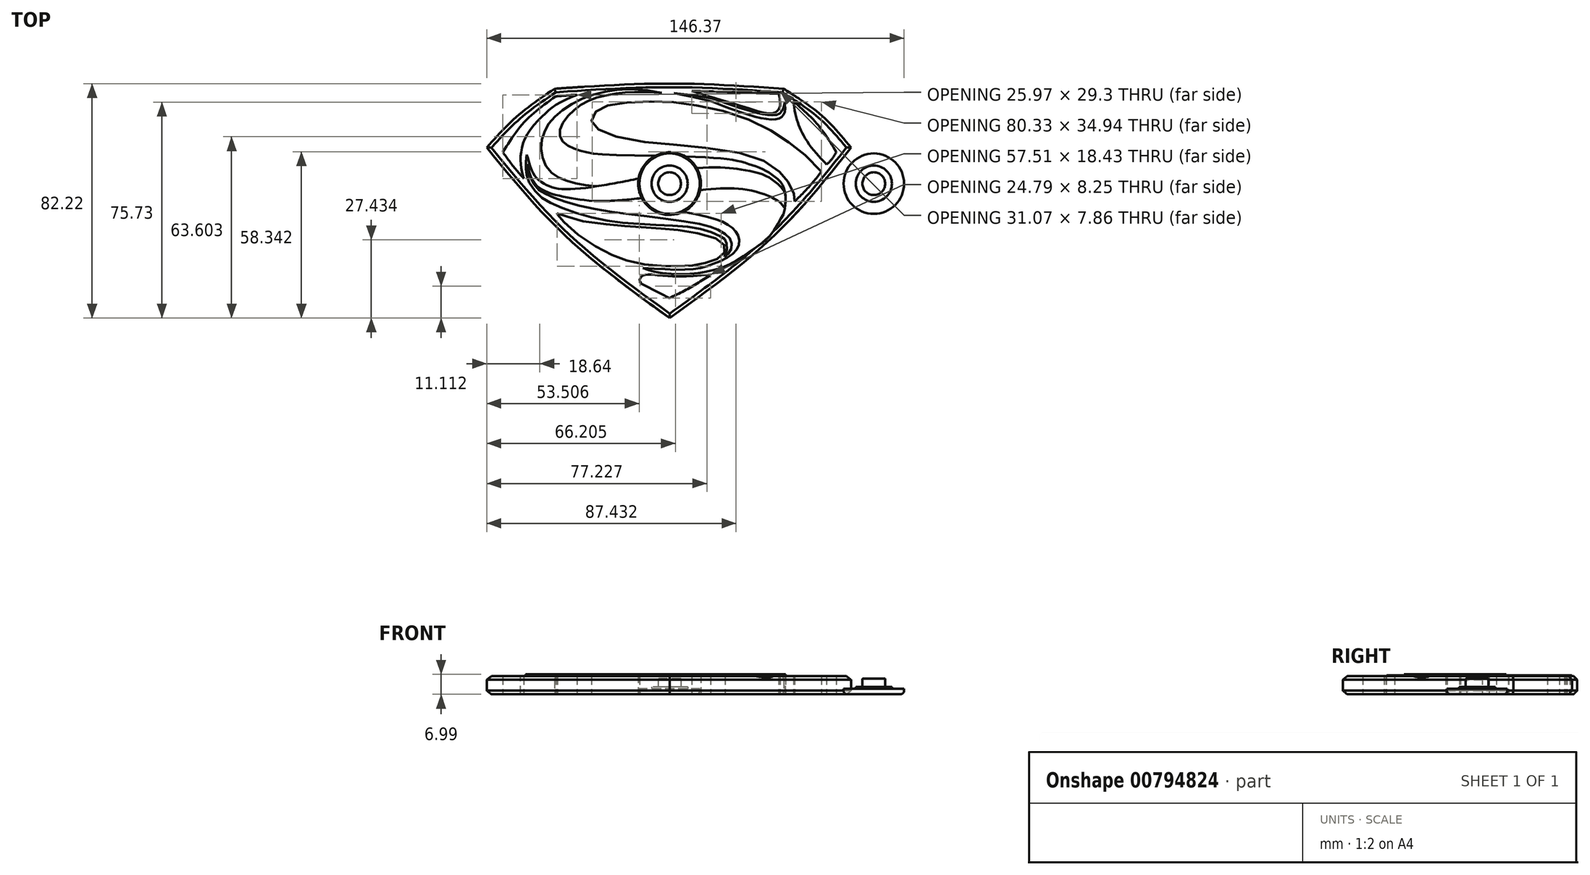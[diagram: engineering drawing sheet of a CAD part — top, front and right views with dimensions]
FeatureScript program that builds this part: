
annotation { "Feature Type Name" : "Feature", "Feature Type Description" : "" }
export const myFeature = defineFeature(function(context is Context, id is Id, definition is map)
    precondition{}
    {
        {
            var Q0;
            Q0=qCreatedBy(makeId("Top.planeOp"),FACE);
            var sketch = newSketch(context, id + "F0", { "sketchPlane" : qUnion([Q0])});
            skCircle(sketch, "E0", {"center": v(0, 0) * mm, "radius": 10.99 * mm});
            skPoint(sketch, "E1", {"position": v(-64.14, 12.66) * mm});
            skPoint(sketch, "E2", {"position": v(-40.37, 33.3) * mm});
            skPoint(sketch, "E3", {"position": v(40.02, 33.3) * mm});
            skPoint(sketch, "E4", {"position": v(63.66, 12.66) * mm});
            skPoint(sketch, "E5", {"position": v(0, -47.12) * mm});
            skPoint(sketch, "E6", {"position": v(7.76, 32.54) * mm});
            skPoint(sketch, "E7", {"position": v(38.28, 31.5) * mm});
            skPoint(sketch, "E8", {"position": v(43.45, 28.9) * mm});
            skPoint(sketch, "E9", {"position": v(55.1, 6.77) * mm});
            skPoint(sketch, "E10", {"position": v(58.48, 11.04) * mm});
            skPoint(sketch, "E11", {"position": v(-51.19, 1.83) * mm});
            skPoint(sketch, "E12", {"position": v(-39.94, 30.62) * mm});
            skPoint(sketch, "E13", {"position": v(-32.52, 31.13) * mm});
            skPoint(sketch, "E14", {"position": v(-39.39, -10.47) * mm});
            skPoint(sketch, "E15", {"position": v(43.9, -6.25) * mm});
            skPoint(sketch, "E16", {"position": v(53.25, 4.2) * mm});
            skPoint(sketch, "E17", {"position": v(14.46, -31.93) * mm});
            skPoint(sketch, "E18", {"position": v(-0.08, -40.13) * mm});
            skPoint(sketch, "E19", {"position": v(-58.48, 11.01) * mm});
            skPoint(sketch, "E20", {"position": v(-50.07, 10.18) * mm});
            skPoint(sketch, "E21", {"position": v(-49.83, 6.88) * mm});
            skPoint(sketch, "E22", {"position": v(19.28, -25.63) * mm});
            skPoint(sketch, "E23", {"position": v(-9.37, -29.55) * mm});
            skPoint(sketch, "E24", {"position": v(40.4, 28.63) * mm});
            skPoint(sketch, "E25", {"position": v(40.4, -8.67) * mm});
            skPoint(sketch, "E26", {"position": v(-2.68, 31.88) * mm});
            skPoint(sketch, "E27", {"position": v(0, 31.88) * mm});
            skFitSpline(sketch, "E28", {"points": [v(-40.37, 33.3) * mm, v(0, 35.1) * mm, v(40.02, 33.3) * mm], "startDerivative": vector(80.66, 5.4) * mm, "endDerivative": vector(80.13, -5.42) * mm});
            skFitSpline(sketch, "E29", {"points": [v(40.02, 33.3) * mm, v(53.16, 24.07) * mm, v(63.66, 12.66) * mm], "startDerivative": vector(27.5, -18.05) * mm, "endDerivative": vector(20.1, -24.17) * mm});
            skFitSpline(sketch, "E30", {"points": [v(63.66, 12.66) * mm, v(36.43, -18.47) * mm, v(0, -47.12) * mm], "startDerivative": vector(-52.44, -66.14) * mm, "endDerivative": vector(-74.66, -53.56) * mm});
            skFitSpline(sketch, "E31", {"points": [v(0, -47.12) * mm, v(-36.36, -18.47) * mm, v(-64.14, 12.66) * mm], "startDerivative": vector(-74.42, 53.78) * mm, "endDerivative": vector(-53.67, 65.9) * mm});
            skFitSpline(sketch, "E32", {"points": [v(-64.14, 12.66) * mm, v(-53.44, 23.64) * mm, v(-40.37, 33.3) * mm], "startDerivative": vector(20.7, 23.07) * mm, "endDerivative": vector(26.78, 18.22) * mm});
            skFitSpline(sketch, "E33", {"points": [v(-39.94, 30.62) * mm, v(-50.69, 21.87) * mm, v(-58.48, 11.01) * mm], "startDerivative": vector(-22.95, -16.13) * mm, "endDerivative": vector(-14.34, -23.1) * mm});
            skFitSpline(sketch, "E34", {"points": [v(-39.94, 30.62) * mm, v(-36.36, 30.92) * mm, v(-32.52, 31.13) * mm], "startDerivative": vector(6.93, 0.72) * mm, "endDerivative": vector(6.91, 0.08) * mm});
            skFitSpline(sketch, "E35", {"points": [v(-58.48, 11.01) * mm, v(-55.4, 6.86) * mm, v(-51.19, 1.83) * mm], "startDerivative": vector(6.2, -8.69) * mm, "endDerivative": vector(8.34, -9.65) * mm});
            skFitSpline(sketch, "E36", {"points": [v(-51.19, 1.83) * mm, v(-51.94, 4.77) * mm, v(-52.27, 8.5) * mm, v(-51.67, 12.97) * mm, v(-49.15, 18.56) * mm, v(-43.9, 24.34) * mm, v(-39.94, 27.57) * mm, v(-32.52, 31.13) * mm], "startDerivative": vector(-7.64, 26.31) * mm, "endDerivative": vector(46.02, 18.09) * mm});
            skFitSpline(sketch, "E37", {"points": [v(7.76, 32.54) * mm, v(18.66, 32.23) * mm, v(38.28, 31.5) * mm], "startDerivative": vector(23.67, -0.62) * mm, "endDerivative": vector(36.73, -1.42) * mm});
            skFitSpline(sketch, "E38", {"points": [v(38.28, 31.5) * mm, v(38.7, 29.67) * mm, v(38.66, 26.9) * mm, v(37.58, 25.39) * mm, v(36.42, 24.79) * mm, v(33.06, 24.83) * mm, v(28.22, 26.27) * mm, v(21.1, 28.47) * mm, v(7.76, 32.54) * mm], "startDerivative": vector(5.44, -19.74) * mm, "endDerivative": vector(-61.62, 18.92) * mm});
            skFitSpline(sketch, "E39", {"points": [v(43.45, 28.9) * mm, v(52.06, 20.57) * mm, v(58.48, 11.04) * mm], "startDerivative": vector(18.08, -15.79) * mm, "endDerivative": vector(11.96, -19.95) * mm});
            skFitSpline(sketch, "E40", {"points": [v(58.48, 11.04) * mm, v(56.98, 8.65) * mm, v(55.1, 6.77) * mm], "startDerivative": vector(-2.74, -4.94) * mm, "endDerivative": vector(-4.03, -3.6) * mm});
            skFitSpline(sketch, "E41", {"points": [v(55.1, 6.77) * mm, v(52.62, 9.33) * mm, v(49.02, 13.7) * mm, v(46.46, 17.85) * mm, v(45.14, 21.05) * mm, v(44.02, 24.73) * mm, v(43.45, 28.9) * mm], "startDerivative": vector(-15.43, 15.4) * mm, "endDerivative": vector(-2.63, 26.61) * mm});
            skFitSpline(sketch, "E42", {"points": [v(14.46, -31.93) * mm, v(7.31, -36.4) * mm, v(-0.08, -40.13) * mm], "startDerivative": vector(-14.08, -9.25) * mm, "endDerivative": vector(-15.01, -7.14) * mm});
            skFitSpline(sketch, "E43", {"points": [v(-0.08, -40.13) * mm, v(-9.4, -35.36) * mm, v(-10.21, -34.82) * mm, v(-10.48, -33.96) * mm, v(-10.15, -32.94) * mm, v(-9.13, -32.13) * mm, v(-7.55, -31.87) * mm, v(-2.45, -32.25) * mm, v(1.98, -32.55) * mm, v(7.03, -32.46) * mm, v(14.46, -31.93) * mm], "startDerivative": vector(-67.8, 34.66) * mm, "endDerivative": vector(3.78, 0.48) * mm});
            skFitSpline(sketch, "E44", {"points": [v(-39.39, -10.47) * mm, v(-36.9, -11.24) * mm, v(-31.58, -12.93) * mm, v(-18.82, -14.57) * mm, v(-12.34, -15.08) * mm, v(-2.67, -15.73) * mm, v(4.94, -16.53) * mm, v(15.15, -18.82) * mm, v(18.68, -20.8) * mm, v(19.36, -22.15) * mm, v(19.36, -23.68) * mm, v(18.1, -25.4) * mm, v(15.6, -26.9) * mm, v(11.3, -28.07) * mm, v(7.09, -28.83) * mm, v(0.64, -28.97) * mm, v(-5.78, -28.66) * mm, v(-14.27, -27.19) * mm, v(-20.2, -24.98) * mm, v(-28.78, -20.23) * mm, v(-36.56, -13.98) * mm, v(-39.24, -10.87) * mm, v(-39.32, -10.74) * mm], "startDerivative": vector(73.96, -20.72) * mm, "endDerivative": vector(-5.97, 11.97) * mm});
            skFitSpline(sketch, "E45", {"points": [v(-39.32, -10.74) * mm, v(-39.39, -10.57) * mm, v(-39.39, -10.47) * mm], "startDerivative": vector(-0.18, 0.22) * mm, "endDerivative": vector(0.04, 0.31) * mm});
            skFitSpline(sketch, "E46", {"points": [v(53.25, 4.2) * mm, v(49.19, -0.76) * mm, v(43.9, -6.25) * mm], "startDerivative": vector(-8.07, -10.34) * mm, "endDerivative": vector(-10.53, -10.36) * mm});
            skFitSpline(sketch, "E47", {"points": [v(43.9, -6.25) * mm, v(43.9, -5.44) * mm, v(43.77, -4.33) * mm, v(43.29, -2.76) * mm, v(41.52, 0.67) * mm, v(39.87, 2.87) * mm, v(35.73, 6.37) * mm, v(27.93, 9.93) * mm, v(7.68, 13.1) * mm, v(-8.05, 14.57) * mm, v(-21.85, 17.4) * mm, v(-25.64, 19.5) * mm, v(-27.06, 21.07) * mm, v(-27.3, 23.07) * mm, v(-26.38, 24.79) * mm, v(-24.06, 26.55) * mm, v(-20.02, 27.79) * mm, v(-11.62, 28.7) * mm, v(-1.38, 28.75) * mm, v(7.82, 27.7) * mm, v(20.5, 25.07) * mm, v(32.34, 20.39) * mm, v(40.34, 15.5) * mm, v(46.38, 11.1) * mm, v(53.25, 4.2) * mm], "startDerivative": vector(4.91, 51.7) * mm, "endDerivative": vector(132.4, -142.33) * mm});
            skFitSpline(sketch, "E48", {"points": [v(40.4, 28.63) * mm, v(40.06, 27.03) * mm, v(39.45, 25.6) * mm, v(38.15, 24.37) * mm, v(35.2, 24.05) * mm, v(31.42, 24.69) * mm, v(24.88, 26.45) * mm, v(19.2, 28.46) * mm, v(14.9, 29.85) * mm, v(8.9, 30.88) * mm, v(1.53, 31.72) * mm], "startDerivative": vector(-3.32, -25.72) * mm, "endDerivative": vector(-54.65, 5.86) * mm});
            skFitSpline(sketch, "E49", {"points": [v(40.4, 28.63) * mm, v(40.5, 27.43) * mm, v(40.52, 25.95) * mm, v(40.2, 24.52) * mm, v(39.55, 23.59) * mm, v(38.69, 22.97) * mm, v(37.25, 22.55) * mm, v(34.59, 22.59) * mm, v(30.57, 23.33) * mm, v(24.5, 25.22) * mm, v(20.17, 26.73) * mm, v(15.83, 28.4) * mm, v(11.85, 29.6) * mm, v(1.53, 31.72) * mm], "startDerivative": vector(3.06, -23.78) * mm, "endDerivative": vector(-90.61, 18.57) * mm});
            skFitSpline(sketch, "E50", {"points": [v(-2.68, 31.88) * mm, v(-7.95, 32.74) * mm, v(-17.45, 32.96) * mm, v(-30.23, 29.97) * mm, v(-39.96, 23.74) * mm, v(-44.1, 17.75) * mm, v(-44.83, 10.28) * mm, v(-41.26, 3.66) * mm, v(-34.87, 0.66) * mm, v(-25.14, -0.98) * mm, v(-17.45, -1.32) * mm, v(-18.98, -2.45) * mm, v(-32.6, -3.3) * mm, v(-31.7, -4.65) * mm, v(-21.24, -6.69) * mm, v(-12.19, -7.76) * mm, v(11.4, -11.16) * mm, v(20.9, -14.67) * mm, v(23.56, -17.32) * mm, v(24.41, -20.66) * mm, v(22.32, -24.45) * mm, v(15.13, -28.24) * mm, v(7.33, -30.05) * mm, v(-9.37, -29.55) * mm], "startDerivative": vector(-142.44, 17.07) * mm, "endDerivative": vector(-293.82, 20.27) * mm});
            skFitSpline(sketch, "E51", {"points": [v(-9.37, -29.55) * mm, v(-4.88, -30.97) * mm, v(5.35, -31.7) * mm, v(14.06, -30.62) * mm, v(21.7, -28.02) * mm, v(29, -23.2) * mm, v(35.18, -18.41) * mm, v(38.8, -12.68) * mm, v(40.21, -9.83) * mm, v(40.16, -1.79) * mm, v(36.4, 2.85) * mm, v(32.12, 5.3) * mm, v(26.56, 7.28) * mm, v(15.88, 9.03) * mm, v(-22.44, 10.23) * mm, v(-29.79, 11.13) * mm, v(-34.2, 12.6) * mm, v(-37.8, 15.33) * mm, v(-38.3, 19.43) * mm, v(-33.85, 25.5) * mm, v(-27.24, 29.56) * mm, v(-17.42, 31.74) * mm, v(-2.68, 31.88) * mm], "startDerivative": vector(111.61, -43.93) * mm, "endDerivative": vector(382.73, -23.2) * mm});
            skFitSpline(sketch, "E52", {"points": [v(40.4, -8.67) * mm, v(40.7, -5.87) * mm, v(40.56, -3.55) * mm, v(39.02, -1.13) * mm, v(35.74, 1.6) * mm, v(31.47, 3.62) * mm, v(24.9, 4.98) * mm, v(19.45, 5.6) * mm, v(8.3, 5.35) * mm, v(-3.53, 3.33) * mm, v(-13.8, 1.18) * mm, v(-22.74, -0.47) * mm, v(-33.27, -1.85) * mm, v(-39.9, -1.61) * mm, v(-42.99, -0.54) * mm, v(-46.25, 1.58) * mm, v(-48.17, 4.27) * mm, v(-50.07, 10.18) * mm], "startDerivative": vector(13.14, 77.38) * mm, "endDerivative": vector(-29.7, 107.37) * mm});
            skFitSpline(sketch, "E53", {"points": [v(-50.07, 10.18) * mm, v(-50.35, 7.84) * mm, v(-50.42, 5.22) * mm, v(-50.15, 3.18) * mm, v(-49.15, 0.24) * mm, v(-46.14, -3.8) * mm, v(-42.38, -6.4) * mm, v(-34.14, -9.81) * mm, v(-22.18, -12.93) * mm, v(-9.5, -14.21) * mm, v(4.26, -14.95) * mm, v(12.52, -16.3) * mm, v(17.32, -18.25) * mm, v(19.08, -19.25) * mm, v(19.64, -19.91) * mm, v(20.02, -21.2) * mm, v(20.08, -22.93) * mm, v(19.28, -25.63) * mm], "startDerivative": vector(-7.56, -53.6) * mm, "endDerivative": vector(-22.29, -60.92) * mm});
            skFitSpline(sketch, "E54", {"points": [v(19.28, -25.63) * mm, v(20.18, -24.97) * mm, v(21.42, -23.31) * mm, v(21.72, -21.43) * mm, v(21.5, -19.71) * mm, v(20.16, -18.13) * mm, v(16.78, -16.11) * mm, v(12.06, -14.45) * mm, v(-5.28, -11.81) * mm, v(-24.12, -9.3) * mm, v(-37.8, -5.93) * mm, v(-43.72, -3.47) * mm, v(-46.44, -1.63) * mm, v(-49, 2.57) * mm, v(-49.52, 4.4) * mm, v(-49.83, 6.88) * mm], "startDerivative": vector(26.73, 16.6) * mm, "endDerivative": vector(-6.33, 54.96) * mm});
            skFitSpline(sketch, "E55", {"points": [v(-49.83, 6.88) * mm, v(-49.04, 3.5) * mm, v(-47.4, 0.29) * mm, v(-45.66, -1.45) * mm, v(-42.08, -3.3) * mm, v(-36.7, -4.66) * mm, v(-30.44, -5.7) * mm, v(-18.92, -5.95) * mm, v(7.7, -2.71) * mm, v(20.26, -1.63) * mm, v(29.3, -2.6) * mm, v(36.52, -5.15) * mm, v(39.24, -7.07) * mm, v(40.4, -8.67) * mm], "startDerivative": vector(10.3, -60.65) * mm, "endDerivative": vector(23.49, -38.16) * mm});
            skSolve(sketch);
        }
        {
            var Q0;
            Q0=makeQuery(id+"F0.imprint","IMPRINT",FACE,{"disambiguationData":[TD([[makeQuery(id+"F0.imprint","IMPRINT",EDGE,{"derivedFrom":sQuery(id+"F0.wireOp",EDGE,"E28")}),-1.0]])]});
            var Q1;
            {var subQ0=sQuery(id+"F0.wireOp",EDGE,"E55");var subQ1=sQuery(id+"F0.wireOp",EDGE,"E0");var subQ2=makeQuery(id+"F0.imprint","INTERSECT",VERTEX,{"disambiguationData":[OD(0.0)],"derivedFrom":[subQ1,subQ0]});Q1=makeQuery(id+"F0.imprint","IMPRINT",FACE,{"disambiguationData":[TD([[makeQuery(id+"F0.imprint","IMPRINT",EDGE,{"disambiguationData":[TD([[subQ2,-1.0]])],"derivedFrom":subQ1}),-1.0]])]});}
            extrude(context, id + "F1", {"entities" : qUnion([Q0, Q1]), "depth" : 6.35 * mm, "offsetDistance" : 25.4 * mm});
        }
        {
            var Q0;
            {var subQ5=sQuery(id+"F0.wireOp",EDGE,"E0");var subQ7=sQuery(id+"F0.wireOp",EDGE,"E50");var subQ9=makeQuery(id+"F0.imprint","INTERSECT",VERTEX,{"disambiguationData":[OD(1.0)],"derivedFrom":[subQ5,subQ7]});Q0=makeQuery(id+"F0.imprint","IMPRINT",FACE,{"disambiguationData":[TD([[makeQuery(id+"F0.imprint","IMPRINT",EDGE,{"disambiguationData":[TD([[subQ9,-1.0]])],"derivedFrom":subQ5}),-1.0]])]});}
            var Q1;
            {var subQ0=sQuery(id+"F0.wireOp",EDGE,"E51");var subQ1=sQuery(id+"F0.wireOp",EDGE,"E0");var subQ2=makeQuery(id+"F0.imprint","INTERSECT",VERTEX,{"disambiguationData":[OD(0.0)],"derivedFrom":[subQ1,subQ0]});Q1=makeQuery(id+"F0.imprint","IMPRINT",FACE,{"disambiguationData":[TD([[makeQuery(id+"F0.imprint","IMPRINT",EDGE,{"disambiguationData":[TD([[subQ2,1.0]])],"derivedFrom":subQ1}),-1.0]])]});}
            var Q2;
            {var subQ0=sQuery(id+"F0.wireOp",EDGE,"E51");var subQ1=sQuery(id+"F0.wireOp",EDGE,"E0");var subQ2=makeQuery(id+"F0.imprint","INTERSECT",VERTEX,{"disambiguationData":[OD(1.0)],"derivedFrom":[subQ1,subQ0]});Q2=makeQuery(id+"F0.imprint","IMPRINT",FACE,{"disambiguationData":[TD([[makeQuery(id+"F0.imprint","IMPRINT",EDGE,{"disambiguationData":[TD([[subQ2,-1.0]])],"derivedFrom":subQ1}),-1.0]])]});}
            var Q3;
            Q3=makeQuery(id+"F0.imprint","IMPRINT",FACE,{"disambiguationData":[TD([[makeQuery(id+"F0.imprint","IMPRINT",EDGE,{"derivedFrom":sQuery(id+"F0.wireOp",EDGE,"E48")}),1.0]])]});
            extrude(context, id + "F2", {"entities" : qUnion([Q0, Q1, Q2, Q3]), "operationType" : NewBodyOperationType.ADD, "depth" : 6.6 * mm, "offsetDistance" : 25.4 * mm});
        }
        {
            var Q0;
            {var subQ1=sQuery(id+"F0.wireOp",EDGE,"E53");Q0=makeQuery(id+"F0.imprint","IMPRINT",FACE,{"disambiguationData":[TD([[makeQuery(id+"F0.imprint","IMPRINT",EDGE,{"derivedFrom":subQ1}),1.0]])]});}
            var Q1;
            {var subQ0=sQuery(id+"F0.wireOp",EDGE,"E52");var subQ1=sQuery(id+"F0.wireOp",EDGE,"E0");var subQ2=makeQuery(id+"F0.imprint","INTERSECT",VERTEX,{"disambiguationData":[OD(1.0)],"derivedFrom":[subQ1,subQ0]});Q1=makeQuery(id+"F0.imprint","IMPRINT",FACE,{"disambiguationData":[TD([[makeQuery(id+"F0.imprint","IMPRINT",EDGE,{"disambiguationData":[TD([[subQ2,-1.0]])],"derivedFrom":subQ1}),-1.0]])]});}
            var Q2;
            {var subQ1=sQuery(id+"F0.wireOp",EDGE,"E52");var subQ5=sQuery(id+"F0.wireOp",EDGE,"E0");var subQ6=makeQuery(id+"F0.imprint","INTERSECT",VERTEX,{"disambiguationData":[OD(0.0)],"derivedFrom":[subQ5,subQ1]});Q2=makeQuery(id+"F0.imprint","IMPRINT",FACE,{"disambiguationData":[TD([[makeQuery(id+"F0.imprint","IMPRINT",EDGE,{"disambiguationData":[TD([[subQ6,1.0]])],"derivedFrom":subQ5}),-1.0]])]});}
            extrude(context, id + "F3", {"entities" : qUnion([Q0, Q1, Q2]), "operationType" : NewBodyOperationType.ADD, "depth" : 7 * mm, "offsetDistance" : 25.4 * mm});
        }
        {
            var Q0;
            Q0=makeQuery(id+"F1.opExtrude","CAP_EDGE",EDGE,{"disambiguationData":[OSD([sQuery(id+"F0.wireOp",EDGE,"E32")])],"isStart":false});
            var Q1;
            Q1=makeQuery(id+"F1.opExtrude","CAP_EDGE",EDGE,{"disambiguationData":[OSD([sQuery(id+"F0.wireOp",EDGE,"E31")])],"isStart":false});
            var Q2;
            Q2=makeQuery(id+"F1.opExtrude","CAP_EDGE",EDGE,{"disambiguationData":[OSD([sQuery(id+"F0.wireOp",EDGE,"E30")])],"isStart":false});
            var Q3;
            Q3=makeQuery(id+"F1.opExtrude","CAP_EDGE",EDGE,{"disambiguationData":[OSD([sQuery(id+"F0.wireOp",EDGE,"E29")])],"isStart":false});
            var Q4;
            Q4=makeQuery(id+"F1.opExtrude","CAP_EDGE",EDGE,{"disambiguationData":[OSD([sQuery(id+"F0.wireOp",EDGE,"E28")])],"isStart":false});
            var Q5;
            Q5=makeQuery(id+"F1.opExtrude","CAP_EDGE",EDGE,{"disambiguationData":[OSD([sQuery(id+"F0.wireOp",EDGE,"E31")])],"isStart":true});
            var Q6;
            Q6=makeQuery(id+"F1.opExtrude","CAP_EDGE",EDGE,{"disambiguationData":[OSD([sQuery(id+"F0.wireOp",EDGE,"E32")])],"isStart":true});
            var Q7;
            Q7=makeQuery(id+"F1.opExtrude","CAP_EDGE",EDGE,{"disambiguationData":[OSD([sQuery(id+"F0.wireOp",EDGE,"E28")])],"isStart":true});
            var Q8;
            Q8=makeQuery(id+"F1.opExtrude","CAP_EDGE",EDGE,{"disambiguationData":[OSD([sQuery(id+"F0.wireOp",EDGE,"E30")])],"isStart":true});
            var Q9;
            Q9=makeQuery(id+"F1.opExtrude","CAP_EDGE",EDGE,{"disambiguationData":[OSD([sQuery(id+"F0.wireOp",EDGE,"E29")])],"isStart":true});
            chamfer(context, id + "F4", {"entities" : qUnion([Q0, Q1, Q2, Q3, Q4, Q5, Q6, Q7, Q8, Q9]), "width" : 1.27 * mm, "tangentPropagation" : true});
        }
        {
            var Q0;
            Q0=qCreatedBy(makeId("Top.planeOp"),FACE);
            var sketch = newSketch(context, id + "F5", { "sketchPlane" : qUnion([Q0])});
            skCircle(sketch, "E56", {"center": v(0, 0) * mm, "radius": 10.6 * mm});
            skCircle(sketch, "E57", {"center": v(0, 0) * mm, "radius": 6.35 * mm});
            skCircle(sketch, "E58", {"center": v(0, 0) * mm, "radius": 4 * mm});
            skSolve(sketch);
        }
        {
            var Q0;
            Q0=makeQuery(id+"F5.imprint","IMPRINT",FACE,{"disambiguationData":[TD([[makeQuery(id+"F5.imprint","IMPRINT",EDGE,{"derivedFrom":sQuery(id+"F5.wireOp",EDGE,"E56")}),1.0]])]});
            extrude(context, id + "F6", {"entities" : qUnion([Q0]), "depth" : 2 * mm, "offsetDistance" : 25.4 * mm});
        }
        {
            var Q0;
            Q0=makeQuery(id+"F5.imprint","IMPRINT",FACE,{"disambiguationData":[TD([[makeQuery(id+"F5.imprint","IMPRINT",EDGE,{"derivedFrom":sQuery(id+"F5.wireOp",EDGE,"E57")}),1.0]])]});
            extrude(context, id + "F7", {"entities" : qUnion([Q0]), "operationType" : NewBodyOperationType.ADD, "depth" : 2.54 * mm, "offsetDistance" : 25.4 * mm});
        }
        {
            var Q0;
            Q0=makeQuery(id+"F5.imprint","IMPRINT",FACE,{"disambiguationData":[TD([[makeQuery(id+"F5.imprint","IMPRINT",EDGE,{"derivedFrom":sQuery(id+"F5.wireOp",EDGE,"E58")}),1.0]])]});
            extrude(context, id + "F8", {"entities" : qUnion([Q0]), "operationType" : NewBodyOperationType.ADD, "depth" : 5.5 * mm, "offsetDistance" : 25.4 * mm});
        }
        {
            var Q0;
            Q0=makeQuery(id+"F6.opExtrude","CAP_EDGE",EDGE,{"disambiguationData":[OSD([sQuery(id+"F5.wireOp",EDGE,"E56")])],"isStart":true});
            fillet(context, id + "F9", {"entities" : qUnion([Q0]), "radius" : 1.27 * mm, "tangentPropagation" : true, "allowEdgeOverflow" : false});
        }
        {
            var Q0;
            Q0=makeQuery(id+"F8.opExtrude","CAP_EDGE",EDGE,{"disambiguationData":[OSD([sQuery(id+"F5.wireOp",EDGE,"E58")])],"isStart":false});
            fillet(context, id + "F10", {"entities" : qUnion([Q0]), "radius" : 0.23 * mm, "tangentPropagation" : true, "allowEdgeOverflow" : false});
        }
        {
            var Q0;
            Q0=makeQuery(id+"F6.opExtrude","SWEPT_BODY",BODY,{"disambiguationData":[OSD([sQuery(id+"F5.wireOp",EDGE,"E56"),sQuery(id+"F5.wireOp",EDGE,"E57")])]});
            transform(context, id + "F11", {"entities" : qUnion([Q0]), "transformType" : TransformType.TRANSLATION_3D, "dx" : 71.63 * mm, "dy" : 0 * mm, "dz" : 0 * mm, "makeCopy" : true});
        }
    });
